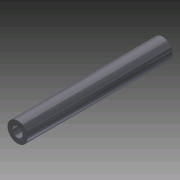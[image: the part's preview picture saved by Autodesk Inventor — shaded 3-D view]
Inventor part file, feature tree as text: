
AUTODESK INVENTOR PART (.ipt)
format: ipt  version: 2011 (Build 150239000, 239)  size: 76,288 bytes
history: native  units: in
note: dims shown in document units (in); Inventor stores cm internally (conversion verified against a paired STEP export)
features: extrude x3, sketch x3
ambient origin geometry x8: Origin, YZ Plane, XZ Plane, XY Plane, X Axis, Y Axis, Z Axis, Center Point
bodies: Solid1 (feature_tree)
feature tree (6):
  extrude  "Extrusion1"  Depth=1.806in TaperAngle=0.0deg
  extrude  "Extrusion2"  Depth=0.25in TaperAngle=0.0deg
  extrude  "Extrusion3"  Depth=0.25in TaperAngle=0.0deg
  sketch  "Sketch1"  dims[d0=0.249in d1=1.806in d2=0.0in]
  sketch  "Sketch2"  dims[d3=0.126in d4=0.25in d5=0.0in]
  sketch  "Sketch3"  dims[d6=0.126in d7=0.25in d8=0.0in]
